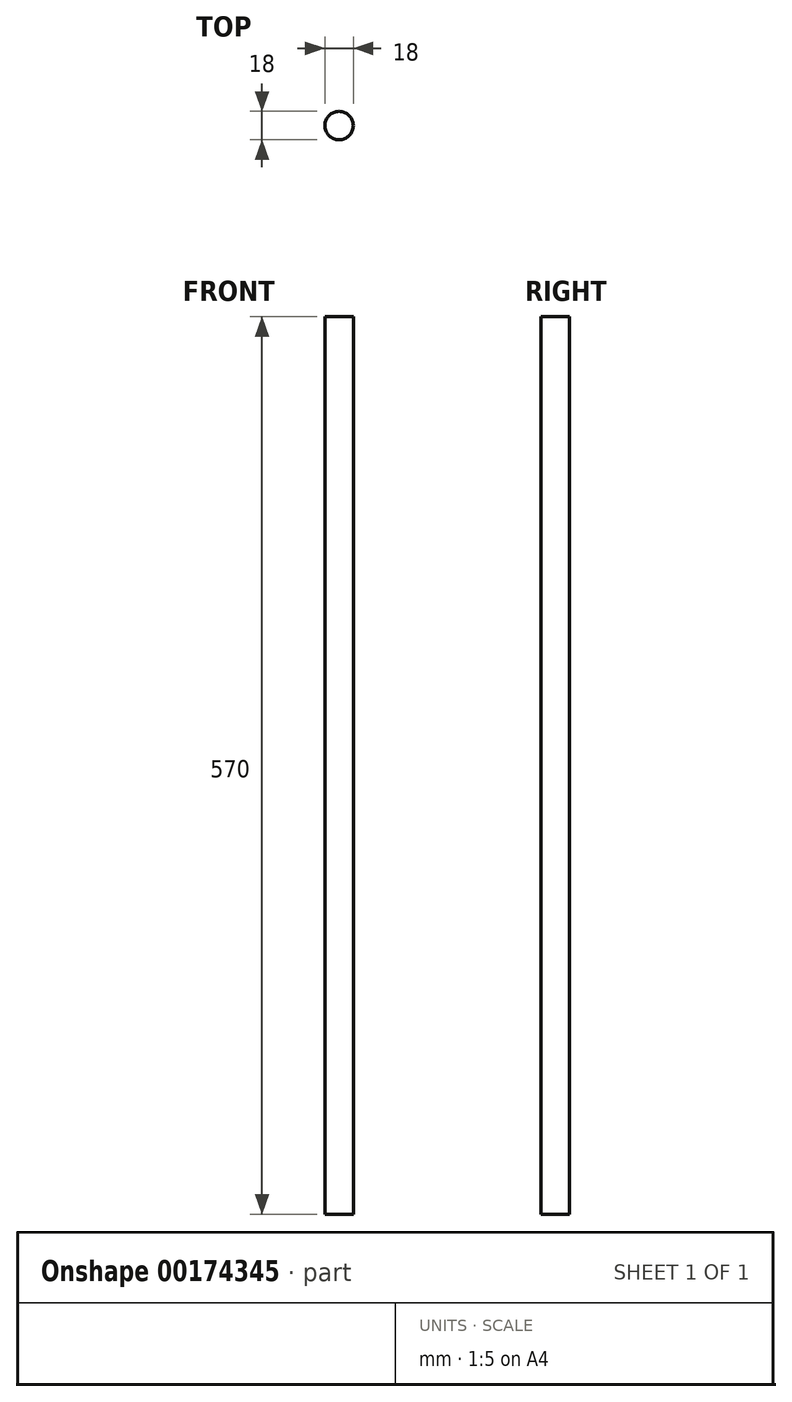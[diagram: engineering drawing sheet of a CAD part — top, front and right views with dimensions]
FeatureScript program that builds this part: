
annotation { "Feature Type Name" : "Feature", "Feature Type Description" : "" }
export const myFeature = defineFeature(function(context is Context, id is Id, definition is map)
    precondition{}
    {
        {
            var Q0;
            Q0=qCreatedBy(makeId("Top.planeOp"),FACE);
            var sketch = newSketch(context, id + "F0", { "sketchPlane" : qUnion([Q0])});
            skCircle(sketch, "E0", {"center": v(0, 0) * mm, "radius": 9 * mm});
            skSolve(sketch);
        }
        {
            var Q0;
            Q0=makeQuery(id+"F0.imprint","IMPRINT",FACE,{"disambiguationData":[TD([[makeQuery(id+"F0.imprint","IMPRINT",EDGE,{"derivedFrom":sQuery(id+"F0.wireOp",EDGE,"E0")}),1.0]])]});
            extrude(context, id + "F1", {"entities" : qUnion([Q0]), "endBound" : BoundingType.SYMMETRIC, "depth" : 570 * mm});
        }
    });
